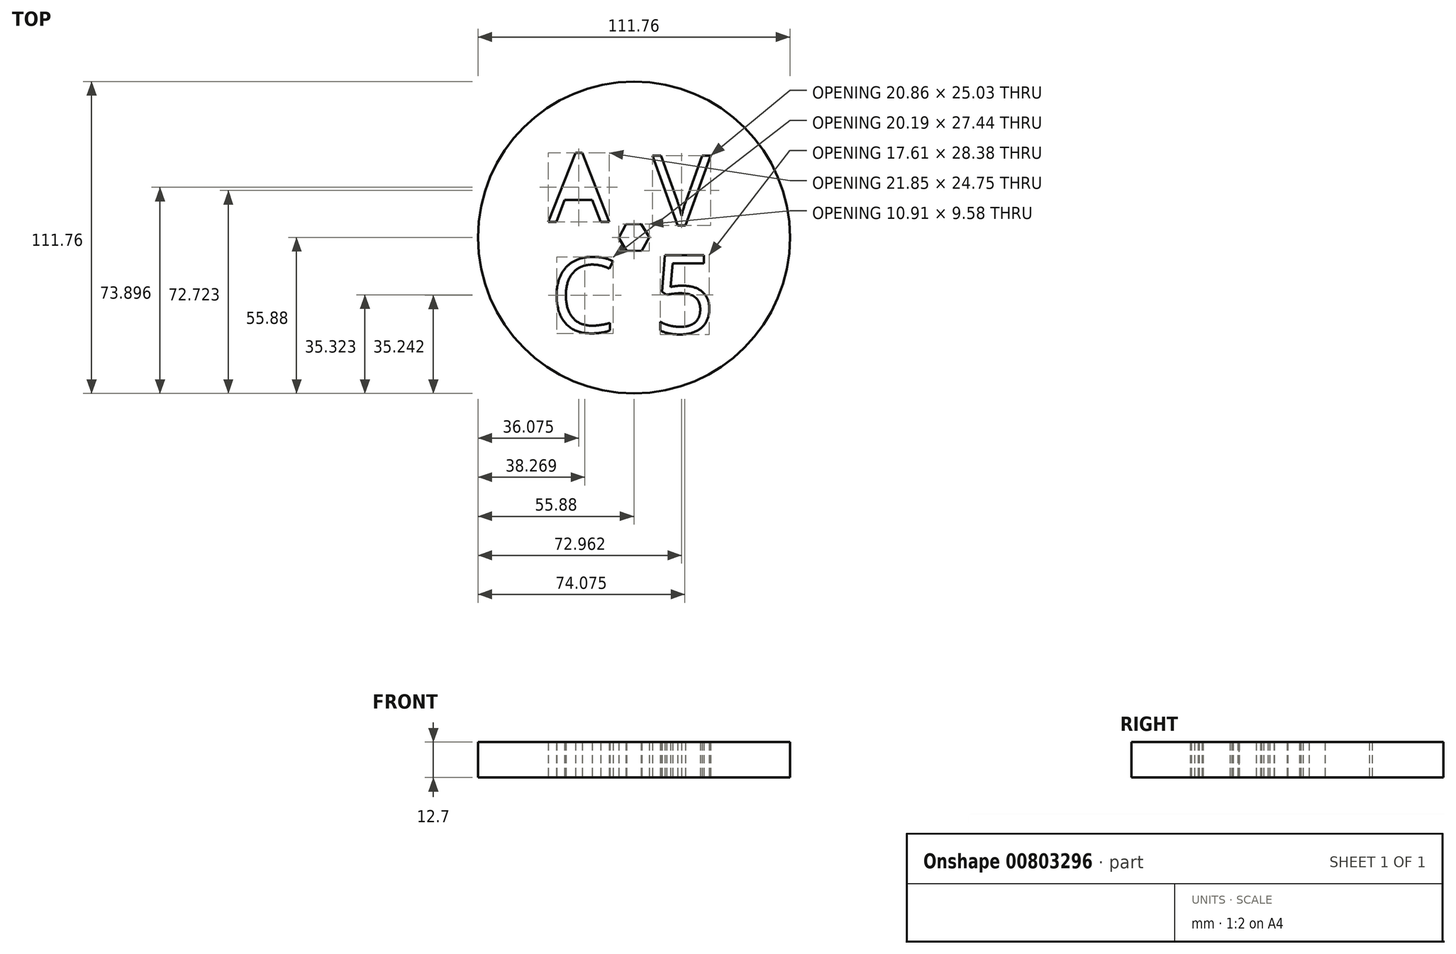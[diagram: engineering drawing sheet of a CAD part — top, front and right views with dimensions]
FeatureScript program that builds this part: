
annotation { "Feature Type Name" : "Feature", "Feature Type Description" : "" }
export const myFeature = defineFeature(function(context is Context, id is Id, definition is map)
    precondition{}
    {
        {
            var Q0;
            Q0=qCreatedBy(makeId("Top.planeOp"),FACE);
            var sketch = newSketch(context, id + "F0", { "sketchPlane" : qUnion([Q0])});
            skCircle(sketch, "E0", {"center": v(0, 0) * mm, "radius": 55.88 * mm});
            skCircle(sketch, "E1.cCircle", {"center": v(0, 0) * mm, "radius": 4.73 * mm, "construction": true});
            skLineSegment(sketch, "E1.0", {"start": v(2.61, 4.8) * mm, "end": v(5.46, 0.13) * mm});
            skLineSegment(sketch, "E1.1", {"start": v(5.46, 0.13) * mm, "end": v(2.84, -4.66) * mm});
            skLineSegment(sketch, "E1.2", {"start": v(2.84, -4.66) * mm, "end": v(-2.61, -4.8) * mm});
            skLineSegment(sketch, "E1.3", {"start": v(-2.61, -4.8) * mm, "end": v(-5.46, -0.13) * mm});
            skLineSegment(sketch, "E1.4", {"start": v(-5.46, -0.13) * mm, "end": v(-2.84, 4.66) * mm});
            skLineSegment(sketch, "E1.5", {"start": v(-2.84, 4.66) * mm, "end": v(2.61, 4.8) * mm});
            skPoint(sketch, "E1.0.midPoint", {"position": v(4.04, 2.46) * mm});
            skText(sketch, "E2", { "text": "A", "fontName": "OpenSans-Regular.ttf"});
            skText(sketch, "E3", { "text": "V", "fontName": "OpenSans-Regular.ttf"});
            skText(sketch, "E4", { "text": "C", "fontName": "OpenSans-Regular.ttf"});
            skText(sketch, "E5", { "text": "5", "fontName": "OpenSans-Regular.ttf"});
            skLineSegment(sketch, "E6", {"start": v(0, 54.43) * mm, "end": v(0, 33.87) * mm});
            skLineSegment(sketch, "E7", {"start": v(-54.47, 0) * mm, "end": v(-34.1, 0) * mm});
            skLineSegment(sketch, "E8", {"start": v(0, -54) * mm, "end": v(0, -33.61) * mm});
            skLineSegment(sketch, "E9", {"start": v(53.76, 0) * mm, "end": v(33.38, 0) * mm});
            const initialGuessF0  = {"E2": [-0.03073, 0.00564, 1, 0, 0.02486], "E3": [0.00665, 0.00433, 1, 0, 0.02524], "E4": [-0.02999, -0.03399, 1, 0, 0.02692], "E5": [0.00684, -0.03436, 1, 0, 0.02823]};
            skSetInitialGuess(sketch, initialGuessF0);
            skSolve(sketch);
        }
        {
            var Q0;
            Q0 = qSketchRegion(id + "F0", true);
            extrude(context, id + "F1", {"entities" : qUnion([Q0]), "depth" : 12.7 * mm, "offsetDistance" : 25.4 * mm});
        }
    });
